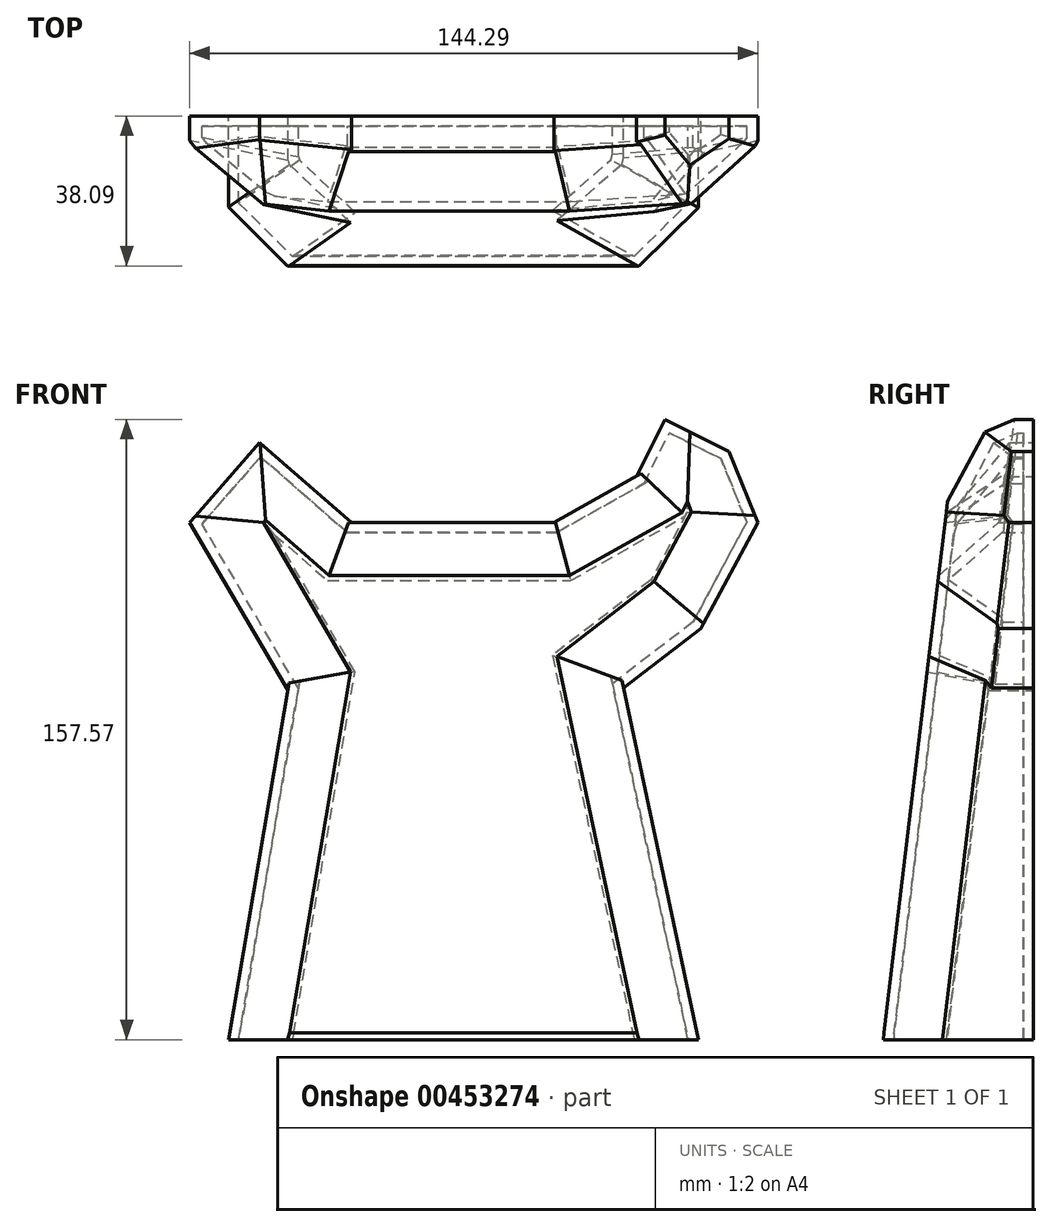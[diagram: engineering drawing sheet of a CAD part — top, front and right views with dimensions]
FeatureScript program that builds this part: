
annotation { "Feature Type Name" : "Feature", "Feature Type Description" : "" }
export const myFeature = defineFeature(function(context is Context, id is Id, definition is map)
    precondition{}
    {
        {
            var Q0;
            Q0=qCreatedBy(makeId("Front.planeOp"),FACE);
            var sketch = newSketch(context, id + "F0", { "sketchPlane" : qUnion([Q0])});
            skLineSegment(sketch, "E0", {"start": v(423.35, 18.03) * mm, "end": v(398.43, 60.66) * mm});
            skLineSegment(sketch, "E1", {"start": v(398.43, 60.66) * mm, "end": v(416.14, 80.99) * mm});
            skLineSegment(sketch, "E2", {"start": v(416.14, 80.99) * mm, "end": v(439.48, 60.66) * mm});
            skLineSegment(sketch, "E3", {"start": v(439.48, 60.66) * mm, "end": v(490.9, 60.66) * mm});
            skLineSegment(sketch, "E4", {"start": v(490.9, 60.66) * mm, "end": v(511.9, 72.46) * mm});
            skLineSegment(sketch, "E5", {"start": v(511.9, 72.46) * mm, "end": v(519.1, 86.9) * mm});
            skLineSegment(sketch, "E6", {"start": v(519.1, 86.9) * mm, "end": v(535.37, 78.76) * mm});
            skLineSegment(sketch, "E7", {"start": v(535.37, 78.76) * mm, "end": v(542.72, 60.66) * mm});
            skLineSegment(sketch, "E8", {"start": v(542.72, 60.66) * mm, "end": v(528.29, 33.77) * mm});
            skLineSegment(sketch, "E9", {"start": v(528.29, 33.77) * mm, "end": v(508.61, 18.68) * mm});
            skLineSegment(sketch, "E10", {"start": v(508.61, 18.68) * mm, "end": v(527.63, -70.68) * mm});
            skLineSegment(sketch, "E11", {"start": v(527.63, -70.68) * mm, "end": v(408.27, -70.68) * mm});
            skLineSegment(sketch, "E12", {"start": v(408.27, -70.68) * mm, "end": v(423.35, 18.03) * mm});
            skSolve(sketch);
        }
        {
            var Q0;
            Q0=makeQuery(id+"F0.imprint","IMPRINT",FACE,{"disambiguationData":[TD([[makeQuery(id+"F0.imprint","IMPRINT",EDGE,{"derivedFrom":sQuery(id+"F0.wireOp",EDGE,"E0")}),-1.0]])]});
            extrude(context, id + "F1", {"entities" : qUnion([Q0]), "depth" : 38.1 * mm});
        }
        {
            var Q0;
            Q0=qCreatedBy(makeId("Right.planeOp"),FACE);
            cPlane(context, id + "F2", {"entities" : qUnion([Q0]), "cplaneType" : CPlaneType.OFFSET, "offset" : 76.2 * mm, "oppositeDirection" : true, "width" : 152.4 * mm, "height" : 152.4 * mm});
        }
        {
            var Q0;
            Q0=qCreatedBy(id+"F2.planeOp",FACE);
            var sketch = newSketch(context, id + "F3", { "sketchPlane" : qUnion([Q0])});
            skLineSegment(sketch, "E13", {"start": v(-38.19, -70.6) * mm, "end": v(0, 248.97) * mm});
            skLineSegment(sketch, "E14", {"start": v(0, 248.97) * mm, "end": v(-45.77, 254.44) * mm});
            skLineSegment(sketch, "E15", {"start": v(-45.77, 254.44) * mm, "end": v(-38.19, -70.6) * mm});
            skSolve(sketch);
        }
        {
            var Q0;
            Q0=qSketchRegion(id+"F3",true);
            extrude(context, id + "F4", {"entities" : qUnion([Q0]), "operationType" : NewBodyOperationType.REMOVE, "endBound" : BoundingType.THROUGH_ALL, "depth" : 25.4 * mm});
        }
        {
            var Q0;
            Q0=makeQuery(id+"F4.boolean.opBoolean","COPY",FACE,{"derivedFrom":makeQuery(id+"F4.opExtrude","SWEPT_FACE",FACE,{"disambiguationData":[OSD([sQuery(id+"F3.wireOp",EDGE,"E13")])]})});
            chamfer(context, id + "F5", {"entities" : qUnion([Q0]), "width" : 15.24 * mm, "tangentPropagation" : true});
        }
        {
            var Q0;
            Q0=makeQuery(id+"F1.opExtrude","SWEPT_FACE",FACE,{"disambiguationData":[OSD([sQuery(id+"F0.wireOp",EDGE,"5UBScBti-lYJG-QWJU-C9wr-LBJ0cxTIyK4E")])]});
            var Q1;
            Q1=makeQuery(id+"F1.opExtrude","SWEPT_FACE",FACE,{"disambiguationData":[OSD([sQuery(id+"F0.wireOp",EDGE,"kee2NxNs-V4EN-bybI-UZDH-BGayg1GiPN7o")])]});
            var Q2;
            Q2=makeQuery(id+"F1.opExtrude","SWEPT_FACE",FACE,{"disambiguationData":[OSD([sQuery(id+"F0.wireOp",EDGE,"E11")])]});
            shell(context, id + "F6", {"entities" : qUnion([Q0, Q1, Q2]), "thickness" : 2.54 * mm});
        }
    });
